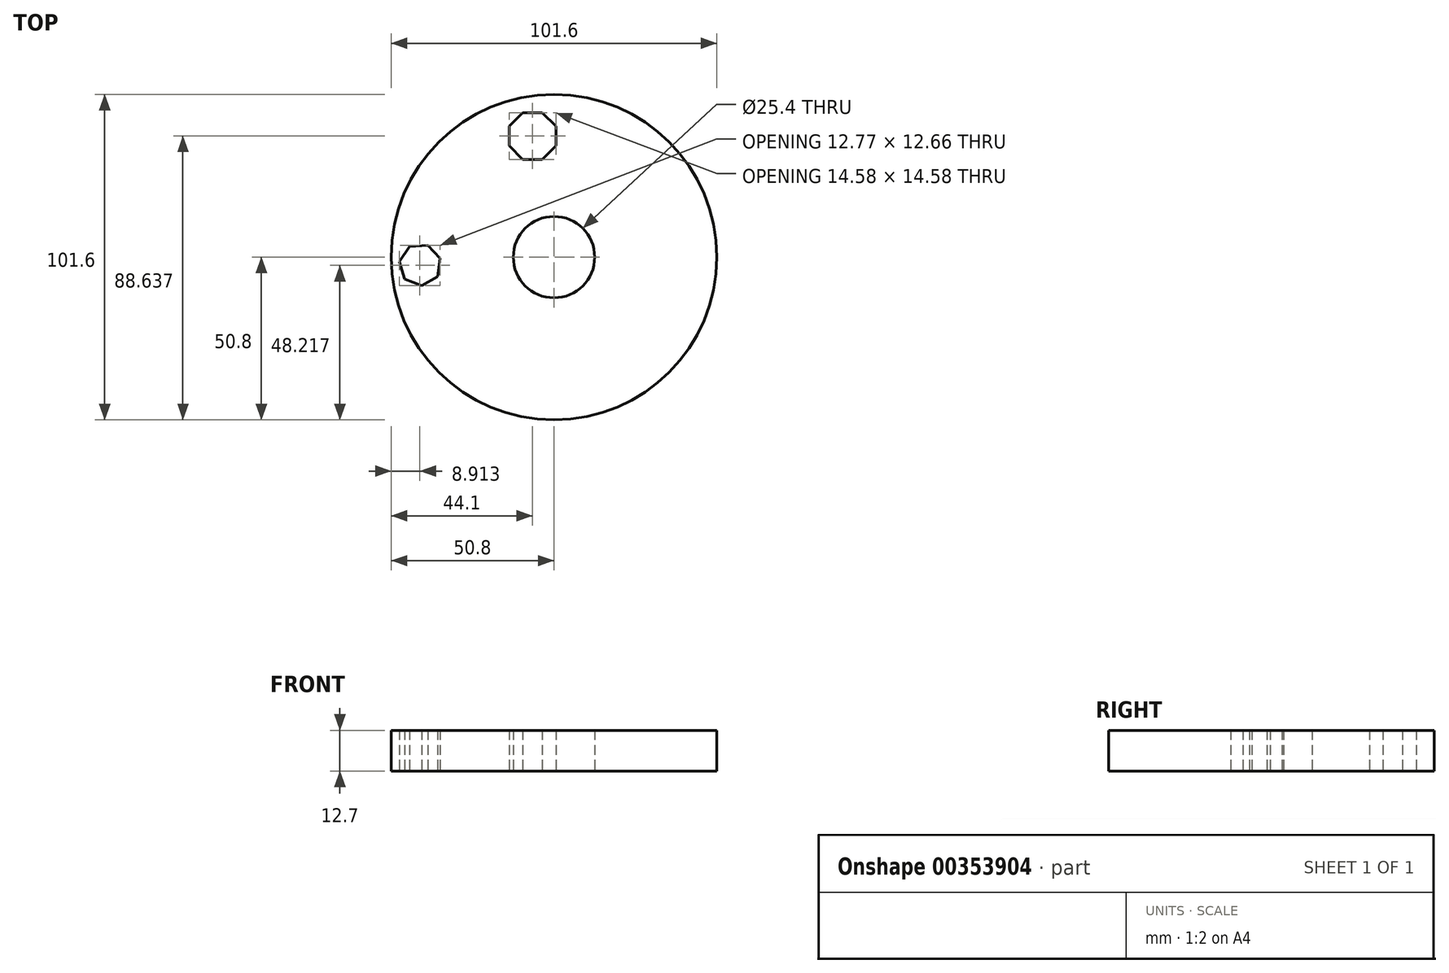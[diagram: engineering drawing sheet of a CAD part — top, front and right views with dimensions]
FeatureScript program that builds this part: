
annotation { "Feature Type Name" : "Feature", "Feature Type Description" : "" }
export const myFeature = defineFeature(function(context is Context, id is Id, definition is map)
    precondition{}
    {
        {
            var Q0;
            Q0=qCreatedBy(makeId("Top.planeOp"),FACE);
            var sketch = newSketch(context, id + "F0", { "sketchPlane" : qUnion([Q0])});
            skCircle(sketch, "E0", {"center": v(0, 0) * mm, "radius": 50.8 * mm});
            skCircle(sketch, "E1", {"center": v(0, 0) * mm, "radius": 12.7 * mm});
            skCircle(sketch, "E2.cCircle", {"center": v(-6.7, 37.84) * mm, "radius": 7.3 * mm, "construction": true});
            skLineSegment(sketch, "E2.0", {"start": v(-3.68, 30.55) * mm, "end": v(-9.72, 30.55) * mm});
            skLineSegment(sketch, "E2.1", {"start": v(-9.72, 30.55) * mm, "end": v(-14, 34.82) * mm});
            skLineSegment(sketch, "E2.2", {"start": v(-14, 34.82) * mm, "end": v(-14, 40.86) * mm});
            skLineSegment(sketch, "E2.3", {"start": v(-14, 40.86) * mm, "end": v(-9.72, 45.13) * mm});
            skLineSegment(sketch, "E2.4", {"start": v(-9.72, 45.13) * mm, "end": v(-3.68, 45.13) * mm});
            skLineSegment(sketch, "E2.5", {"start": v(-3.68, 45.13) * mm, "end": v(0.6, 40.86) * mm});
            skLineSegment(sketch, "E2.6", {"start": v(0.6, 40.86) * mm, "end": v(0.6, 34.82) * mm});
            skLineSegment(sketch, "E2.7", {"start": v(0.6, 34.82) * mm, "end": v(-3.68, 30.55) * mm});
            skPoint(sketch, "E2.0.midPoint", {"position": v(-6.7, 30.55) * mm});
            skCircle(sketch, "E3.cCircle", {"center": v(-41.78, -2.36) * mm, "radius": 5.92 * mm, "construction": true});
            skLineSegment(sketch, "E3.0", {"start": v(-36.36, -6.07) * mm, "end": v(-41.3, -8.91) * mm});
            skLineSegment(sketch, "E3.1", {"start": v(-41.3, -8.91) * mm, "end": v(-46.6, -6.83) * mm});
            skLineSegment(sketch, "E3.2", {"start": v(-46.6, -6.83) * mm, "end": v(-48.27, -1.38) * mm});
            skLineSegment(sketch, "E3.3", {"start": v(-48.27, -1.38) * mm, "end": v(-45.06, 3.32) * mm});
            skLineSegment(sketch, "E3.4", {"start": v(-45.06, 3.32) * mm, "end": v(-39.38, 3.75) * mm});
            skLineSegment(sketch, "E3.5", {"start": v(-39.38, 3.75) * mm, "end": v(-35.5, -0.43) * mm});
            skLineSegment(sketch, "E3.6", {"start": v(-35.5, -0.43) * mm, "end": v(-36.36, -6.07) * mm});
            skPoint(sketch, "E3.0.midPoint", {"position": v(-38.82, -7.49) * mm});
            skSolve(sketch);
        }
        {
            var Q0;
            Q0=makeQuery(id+"F0.imprint","IMPRINT",FACE,{"disambiguationData":[TD([[makeQuery(id+"F0.imprint","IMPRINT",EDGE,{"derivedFrom":sQuery(id+"F0.wireOp",EDGE,"E0")}),1.0]])]});
            extrude(context, id + "F1", {"entities" : qUnion([Q0]), "depth" : 12.7 * mm});
        }
    });
